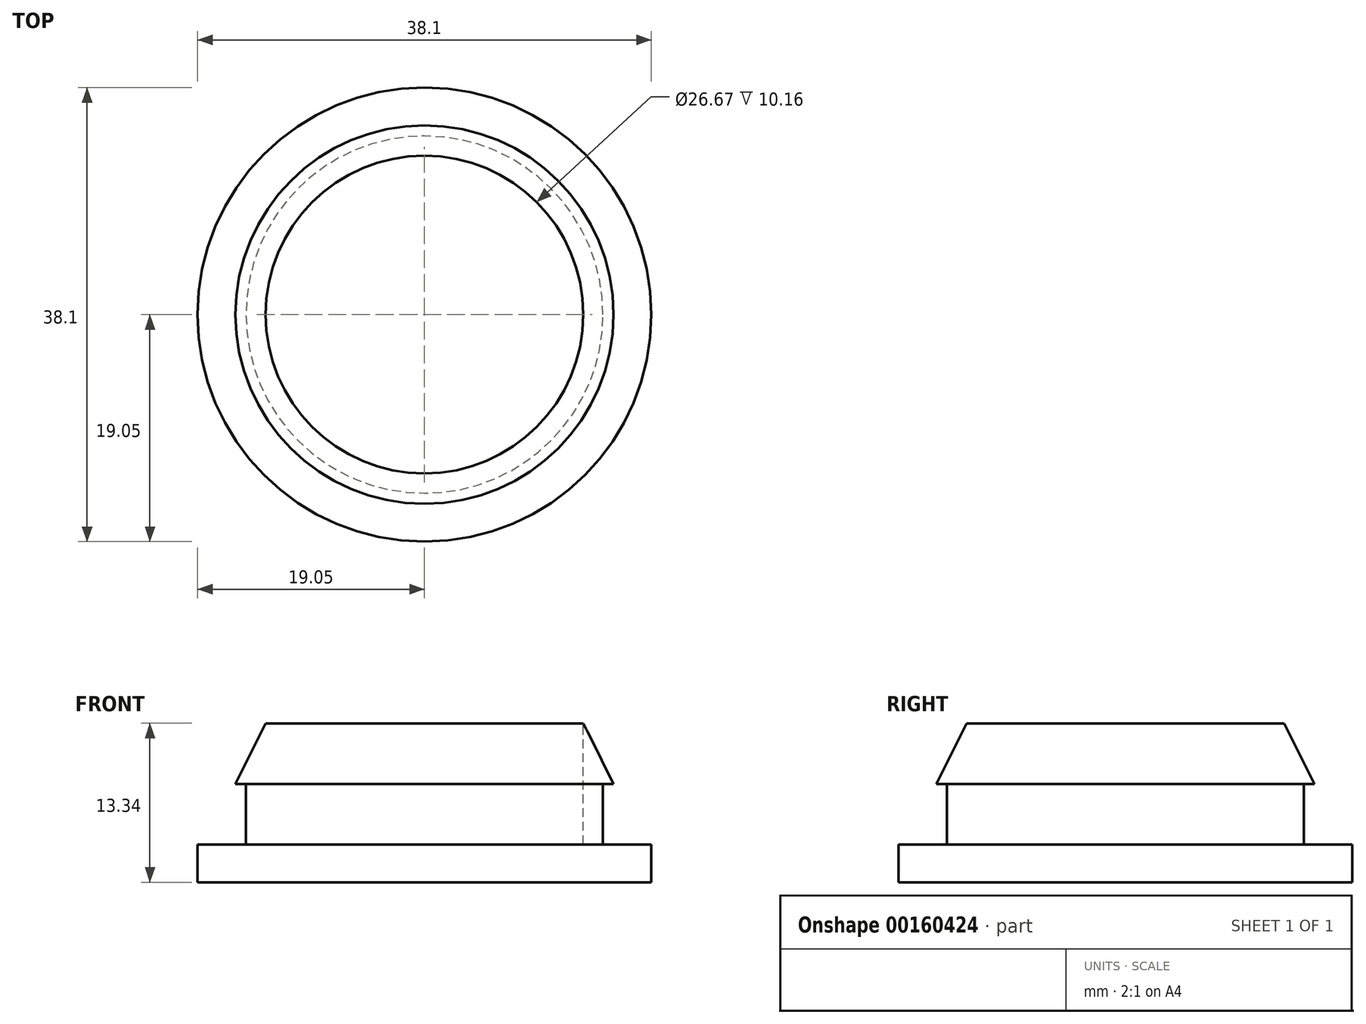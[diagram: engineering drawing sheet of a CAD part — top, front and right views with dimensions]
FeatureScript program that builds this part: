
annotation { "Feature Type Name" : "Feature", "Feature Type Description" : "" }
export const myFeature = defineFeature(function(context is Context, id is Id, definition is map)
    precondition{}
    {
        {
            var Q0;
            Q0=qCreatedBy(makeId("Top.planeOp"),FACE);
            var sketch = newSketch(context, id + "F0", { "sketchPlane" : qUnion([Q0])});
            skCircle(sketch, "E0", {"center": v(0, 0) * mm, "radius": 19.05 * mm});
            skSolve(sketch);
        }
        {
            var Q0;
            Q0 = qSketchRegion(id + "F0", true);
            extrude(context, id + "F1", {"entities" : qUnion([Q0]), "depth" : 3.17 * mm});
        }
        {
            var Q0;
            Q0=makeQuery(id+"F1.opExtrude","CAP_FACE",FACE,{"disambiguationData":[OSD([sQuery(id+"F0.wireOp",EDGE,"E0")])],"isStart":false});
            var sketch = newSketch(context, id + "F2", { "sketchPlane" : qUnion([Q0])});
            skCircle(sketch, "E1", {"center": v(0, 0) * mm, "radius": 14.99 * mm});
            skSolve(sketch);
        }
        {
            var Q0;
            Q0 = qSketchRegion(id + "F2", true);
            extrude(context, id + "F3", {"entities" : qUnion([Q0]), "operationType" : NewBodyOperationType.ADD, "depth" : 5.08 * mm});
        }
        {
            var Q0;
            Q0=makeQuery(id+"F3.opExtrude","CAP_FACE",FACE,{"disambiguationData":[OSD([sQuery(id+"F2.wireOp",EDGE,"E1")])],"isStart":false});
            var sketch = newSketch(context, id + "F4", { "sketchPlane" : qUnion([Q0])});
            skCircle(sketch, "E2", {"center": v(0, 0) * mm, "radius": 15.88 * mm});
            skSolve(sketch);
        }
        {
            var Q0;
            Q0 = qSketchRegion(id + "F4", true);
            extrude(context, id + "F5", {"entities" : qUnion([Q0]), "operationType" : NewBodyOperationType.ADD, "depth" : 5.08 * mm});
        }
        {
            var Q0;
            Q0=makeQuery(id+"F5.opExtrude","CAP_EDGE",EDGE,{"disambiguationData":[OSD([sQuery(id+"F4.wireOp",EDGE,"E2")])],"isStart":false});
            chamfer(context, id + "F6", {"entities" : qUnion([Q0]), "chamferType" : ChamferType.TWO_OFFSETS, "width1" : 2.54 * mm, "oppositeDirection" : false, "width2" : 5.08 * mm, "tangentPropagation" : true});
        }
        {
            var Q0;
            Q0=makeQuery(id+"F5.opExtrude","CAP_FACE",FACE,{"disambiguationData":[OSD([sQuery(id+"F4.wireOp",EDGE,"E2")])],"isStart":false});
            extrude(context, id + "F7", {"entities" : qUnion([Q0]), "operationType" : NewBodyOperationType.REMOVE, "oppositeDirection" : true, "depth" : 10.16 * mm});
        }
    });
